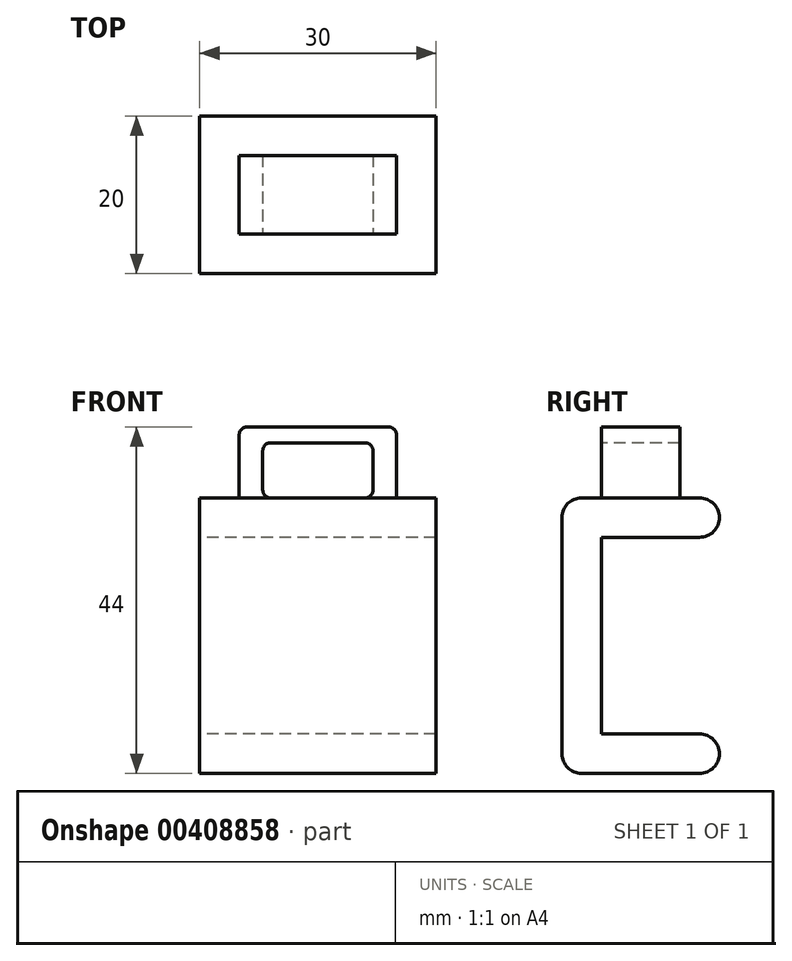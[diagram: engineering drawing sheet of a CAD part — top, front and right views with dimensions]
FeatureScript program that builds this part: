
annotation { "Feature Type Name" : "Feature", "Feature Type Description" : "" }
export const myFeature = defineFeature(function(context is Context, id is Id, definition is map)
    precondition{}
    {
        {
            var Q0;
            Q0=qCreatedBy(makeId("Right.planeOp"),FACE);
            var sketch = newSketch(context, id + "F0", { "sketchPlane" : qUnion([Q0])});
            skLineSegment(sketch, "E0", {"start": v(15, 17.5) * mm, "end": v(15, 12.5) * mm});
            skLineSegment(sketch, "E1", {"start": v(15, 12.5) * mm, "end": v(0, 12.5) * mm});
            skLineSegment(sketch, "E2", {"start": v(0, 12.5) * mm, "end": v(0, -12.5) * mm});
            skLineSegment(sketch, "E3", {"start": v(0, -12.5) * mm, "end": v(15, -12.5) * mm});
            skLineSegment(sketch, "E4", {"start": v(15, -12.5) * mm, "end": v(15, -17.5) * mm});
            skLineSegment(sketch, "E5", {"start": v(15, -17.5) * mm, "end": v(-5, -17.5) * mm});
            skLineSegment(sketch, "E6", {"start": v(-5, -17.5) * mm, "end": v(-5, 17.5) * mm});
            skLineSegment(sketch, "E7", {"start": v(-5, 17.5) * mm, "end": v(15, 17.5) * mm});
            skSolve(sketch);
        }
        {
            var Q0;
            Q0=makeQuery(id+"F0.imprint","IMPRINT",FACE,{"disambiguationData":[TD([[makeQuery(id+"F0.imprint","IMPRINT",EDGE,{"derivedFrom":sQuery(id+"F0.wireOp",EDGE,"E0")}),-1.0]])]});
            extrude(context, id + "F1", {"entities" : qUnion([Q0]), "endBound" : BoundingType.SYMMETRIC, "depth" : 30 * mm});
        }
        {
            var Q0;
            Q0=makeQuery(id+"F1.opExtrude","SWEPT_FACE",FACE,{"disambiguationData":[OSD([sQuery(id+"F0.wireOp",EDGE,"E7")])]});
            var sketch = newSketch(context, id + "F2", { "sketchPlane" : qUnion([Q0])});
            skLineSegment(sketch, "E8.bottom", {"start": v(-10, 10) * mm, "end": v(10, 10) * mm});
            skLineSegment(sketch, "E8.top", {"start": v(-10, 0) * mm, "end": v(10, 0) * mm});
            skLineSegment(sketch, "E8.left", {"start": v(-10, 10) * mm, "end": v(-10, 0) * mm});
            skLineSegment(sketch, "E8.right", {"start": v(10, 10) * mm, "end": v(10, 0) * mm});
            skSolve(sketch);
        }
        {
            var Q0;
            Q0 = qSketchRegion(id + "F2", true);
            extrude(context, id + "F3", {"entities" : qUnion([Q0]), "operationType" : NewBodyOperationType.ADD, "depth" : 9 * mm});
        }
        {
            var Q0;
            Q0=makeQuery(id+"F1.opExtrude","SWEPT_EDGE",EDGE,{"disambiguationData":[OSD([sQuery(id+"F0.wireOp",EDGE,"E0"),sQuery(id+"F0.wireOp",EDGE,"E1")])]});
            var Q1;
            Q1=makeQuery(id+"F1.opExtrude","SWEPT_EDGE",EDGE,{"disambiguationData":[OSD([sQuery(id+"F0.wireOp",EDGE,"E3"),sQuery(id+"F0.wireOp",EDGE,"E4")])]});
            var Q2;
            Q2=makeQuery(id+"F1.opExtrude","SWEPT_EDGE",EDGE,{"disambiguationData":[OSD([sQuery(id+"F0.wireOp",EDGE,"E0"),sQuery(id+"F0.wireOp",EDGE,"E7")])]});
            var Q3;
            Q3=makeQuery(id+"F1.opExtrude","SWEPT_EDGE",EDGE,{"disambiguationData":[OSD([sQuery(id+"F0.wireOp",EDGE,"E4"),sQuery(id+"F0.wireOp",EDGE,"E5")])]});
            var Q4;
            Q4=makeQuery(id+"F1.opExtrude","SWEPT_EDGE",EDGE,{"disambiguationData":[OSD([sQuery(id+"F0.wireOp",EDGE,"E6"),sQuery(id+"F0.wireOp",EDGE,"E7")])]});
            var Q5;
            Q5=makeQuery(id+"F1.opExtrude","SWEPT_EDGE",EDGE,{"disambiguationData":[OSD([sQuery(id+"F0.wireOp",EDGE,"E5"),sQuery(id+"F0.wireOp",EDGE,"E6")])]});
            fillet(context, id + "F4", {"entities" : qUnion([Q0, Q1, Q2, Q3, Q4, Q5]), "radius" : 2.5 * mm, "tangentPropagation" : true, "allowEdgeOverflow" : false});
        }
        {
            var Q0;
            Q0=makeQuery(id+"F3.opExtrude","SWEPT_FACE",FACE,{"disambiguationData":[OSD([sQuery(id+"F2.wireOp",EDGE,"E8.top")])]});
            var sketch = newSketch(context, id + "F5", { "sketchPlane" : qUnion([Q0])});
            skLineSegment(sketch, "E9.bottom", {"start": v(-7, 24.5) * mm, "end": v(7, 24.5) * mm});
            skLineSegment(sketch, "E9.top", {"start": v(-7, 17.5) * mm, "end": v(7, 17.5) * mm});
            skLineSegment(sketch, "E9.left", {"start": v(-7, 24.5) * mm, "end": v(-7, 17.5) * mm});
            skLineSegment(sketch, "E9.right", {"start": v(7, 24.5) * mm, "end": v(7, 17.5) * mm});
            skSolve(sketch);
        }
        {
            var Q0;
            Q0=makeQuery(id+"F5.imprint","IMPRINT",FACE,{"disambiguationData":[TD([[makeQuery(id+"F5.imprint","IMPRINT",EDGE,{"derivedFrom":sQuery(id+"F5.wireOp",EDGE,"E9.bottom")}),-1.0]])]});
            extrude(context, id + "F6", {"entities" : qUnion([Q0]), "operationType" : NewBodyOperationType.REMOVE, "endBound" : BoundingType.UP_TO_NEXT, "oppositeDirection" : true, "depth" : 25 * mm});
        }
        {
            var Q0;
            Q0=makeQuery(id+"F6.boolean.opBoolean","COPY",EDGE,{"derivedFrom":makeQuery(id+"F6.opExtrude","SWEPT_EDGE",EDGE,{"disambiguationData":[OSD([sQuery(id+"F2.wireOp",EDGE,"E8.top"),sQuery(id+"F5.wireOp",EDGE,"E9.top"),sQuery(id+"F5.wireOp",EDGE,"E9.left")])]})});
            var Q1;
            Q1=makeQuery(id+"F6.boolean.opBoolean","COPY",EDGE,{"derivedFrom":makeQuery(id+"F6.opExtrude","SWEPT_EDGE",EDGE,{"disambiguationData":[OSD([sQuery(id+"F5.wireOp",EDGE,"E9.bottom"),sQuery(id+"F5.wireOp",EDGE,"E9.left")])]})});
            var Q2;
            Q2=makeQuery(id+"F6.boolean.opBoolean","COPY",EDGE,{"derivedFrom":makeQuery(id+"F6.opExtrude","SWEPT_EDGE",EDGE,{"disambiguationData":[OSD([sQuery(id+"F2.wireOp",EDGE,"E8.top"),sQuery(id+"F5.wireOp",EDGE,"E9.top"),sQuery(id+"F5.wireOp",EDGE,"E9.right")])]})});
            var Q3;
            Q3=makeQuery(id+"F6.boolean.opBoolean","COPY",EDGE,{"derivedFrom":makeQuery(id+"F6.opExtrude","SWEPT_EDGE",EDGE,{"disambiguationData":[OSD([sQuery(id+"F5.wireOp",EDGE,"E9.bottom"),sQuery(id+"F5.wireOp",EDGE,"E9.right")])]})});
            var Q4;
            Q4=makeQuery(id+"F3.opExtrude","CAP_EDGE",EDGE,{"disambiguationData":[OSD([sQuery(id+"F2.wireOp",EDGE,"E8.left")])],"isStart":true});
            var Q5;
            Q5=makeQuery(id+"F3.opExtrude","CAP_EDGE",EDGE,{"disambiguationData":[OSD([sQuery(id+"F2.wireOp",EDGE,"E8.left")])],"isStart":false});
            var Q6;
            Q6=makeQuery(id+"F3.opExtrude","CAP_EDGE",EDGE,{"disambiguationData":[OSD([sQuery(id+"F2.wireOp",EDGE,"E8.right")])],"isStart":false});
            var Q7;
            Q7=makeQuery(id+"F3.opExtrude","CAP_EDGE",EDGE,{"disambiguationData":[OSD([sQuery(id+"F2.wireOp",EDGE,"E8.right")])],"isStart":true});
            fillet(context, id + "F7", {"entities" : qUnion([Q0, Q1, Q2, Q3, Q4, Q5, Q6, Q7]), "radius" : 1 * mm, "tangentPropagation" : true, "allowEdgeOverflow" : false});
        }
    });
